# Revit family: Door-Crossing-Gard-Grille_Ceiling-Hosted_CornellIron
name_source: partatom
category: Doors
revit_build: Autodesk Revit MEP 2013 (Build: 20130531_2115(x64)
units: mm (PartAtom-declared; Revit-internal decimal feet)

## types (1)
- Door-Crossing-Gard-Grille_Ceiling-Hosted_CornellIron
    04 CSI = 08 33 00
    95 CSI = 08330
    Assembly Code = B2030410
    Bottom Bar (Follows curtain) = Aluminum, mill finish(non-curtain components)
    Coil Dimension Note = 3In to 4 1/2In wide. Consult Cornell when dimensions are critical.
    Curtain Rods 2" OC Standard = Aluminum, anodized finish 9" Spacing (curtain only)
    Curtain Spacing Vertical Chains 3" OC = No
    Curtain Spacing Vertical Chains 6" OC, or = No
    Curtain Spacing Vertical Chains 9" OC, or = No
    Description = The security of a locked rolling grille that opens on alarm or power failure allowing safe escape.
    Distributor Locator = http://www.cornelliron.com
    From Coil Side Operate on Left = No
    From Coil Side Operate on Right = Yes
    Function = Interior
    Guides (Follows curtain) = Aluminum, mill finish(non-curtain components)
    Height = 10' - 0"
    Hood = Aluminum, mill finish(non-curtain components)
    Jamb Dimension Note = 5 1/2In to 6 1/2In wide. Consult Cornell when dimensions are critical.
    LEED Information = http://www.cornelliron.com
    Listings = ICC-ES Evaluated for access controlled egress per the IBC®, per ESR-1167
    Manufacturer = Cornell Iron Works
    Model = ERG-IBC
    Mounting = Face of Wall
    Operator = Operator : Motor Operator
    Optional aluminum, color anodized finish = Aluminum, mill finish(non-curtain components)
    Overall Height = 11' - 10"
    Representative Disclaimer = Cornell products are sold and installed through a nationwide network of independent distributors.
    Revit Object Download Link = http://cornellcookson.smartbim.com
    Sizing Disclaimer = Openings from 5' to 24' wide and 4' to 20' high.
    Subcategory = Roll Up
    URL = http://www.cornelliron.com
    URL CAD = http://www.cornelliron.com
    URL Photographs = http://www.cornelliron.com
    URL Specifications = http://www.cornelliron.com
    Wall Construction = Self supporting tubes, Masonry, Steel or Wood
    Width = 10' - 0"

## geometry (parser evidence)
native form markers: Blend x10, Sweep x13
no freeform markers — native parametric forms only
